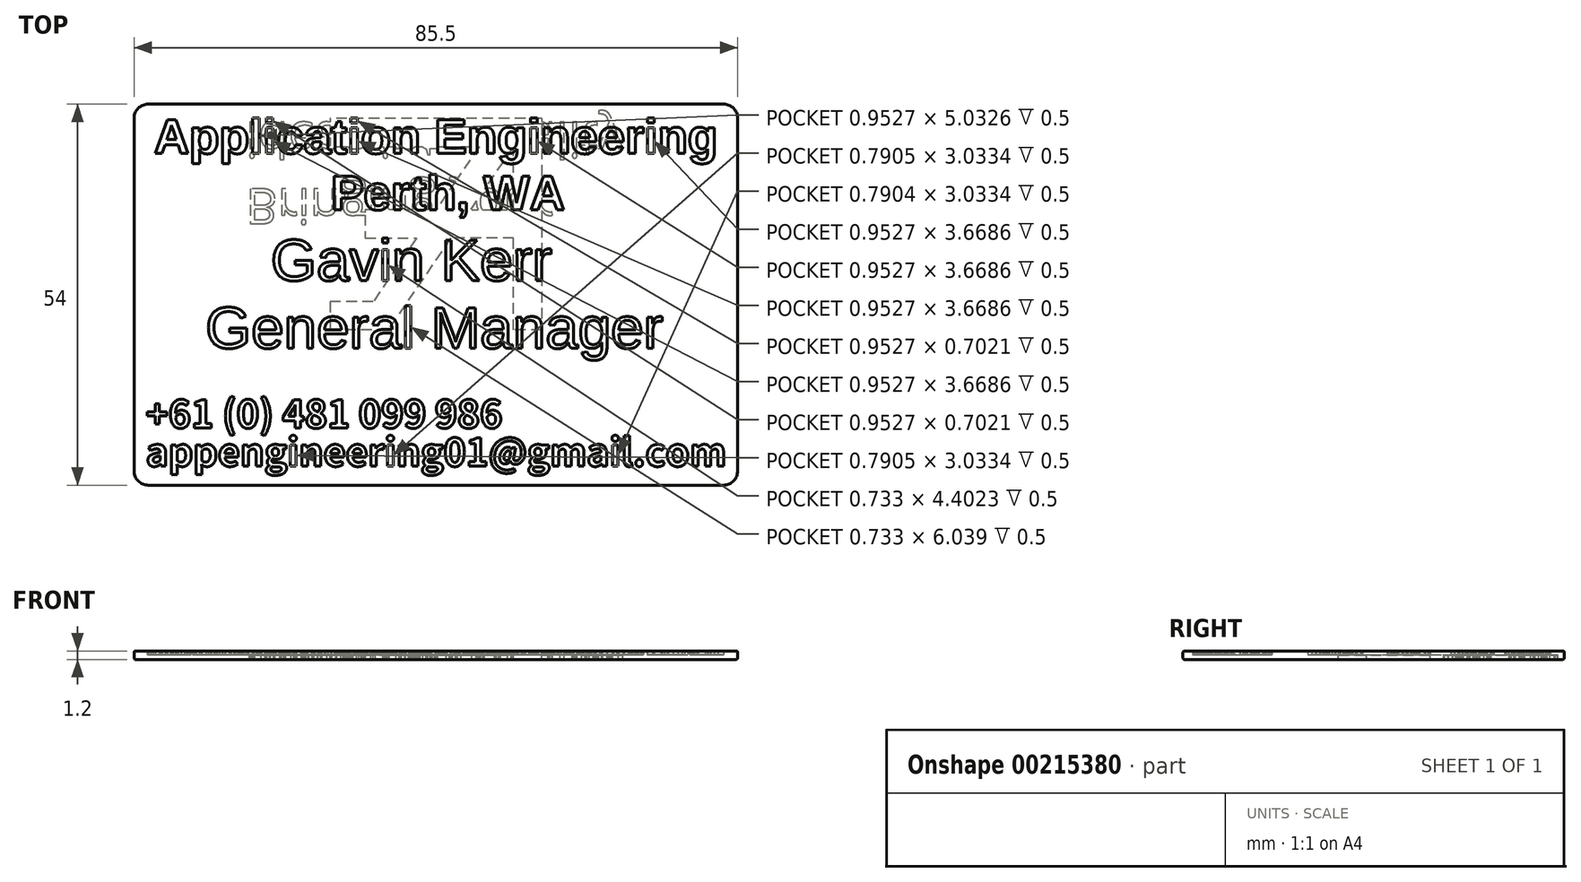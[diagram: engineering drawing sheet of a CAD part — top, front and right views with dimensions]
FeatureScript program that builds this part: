
annotation { "Feature Type Name" : "Feature", "Feature Type Description" : "" }
export const myFeature = defineFeature(function(context is Context, id is Id, definition is map)
    precondition{}
    {
        {
            var Q0;
            Q0=qCreatedBy(makeId("Top.planeOp"),FACE);
            var sketch = newSketch(context, id + "F0", { "sketchPlane" : qUnion([Q0])});
            skLineSegment(sketch, "E0.bottom", {"start": v(40.75, 27) * mm, "end": v(-40.75, 27) * mm});
            skLineSegment(sketch, "E0.top", {"start": v(40.75, -27) * mm, "end": v(-40.75, -27) * mm});
            skLineSegment(sketch, "E0.left", {"start": v(42.75, 25) * mm, "end": v(42.75, -25) * mm});
            skLineSegment(sketch, "E0.right", {"start": v(-42.75, 25) * mm, "end": v(-42.75, -25) * mm});
            skPoint(sketch, "E0.middle", {"position": v(0, 0) * mm});
            skPoint(sketch, "E1.visualSharp", {"position": v(-42.75, 27) * mm});
            skArc(sketch, "E1.filletArc", {"start": v(-40.75, 27) * mm, "mid": v(-42.16, 26.41) * mm, "end": v(-42.75, 25) * mm});
            skPoint(sketch, "E2.visualSharp", {"position": v(42.75, 27) * mm});
            skArc(sketch, "E2.filletArc", {"start": v(42.75, 25) * mm, "mid": v(42.16, 26.41) * mm, "end": v(40.75, 27) * mm});
            skPoint(sketch, "E3.visualSharp", {"position": v(42.75, -27) * mm});
            skArc(sketch, "E3.filletArc", {"start": v(40.75, -27) * mm, "mid": v(42.16, -26.41) * mm, "end": v(42.75, -25) * mm});
            skPoint(sketch, "E4.visualSharp", {"position": v(-42.75, -27) * mm});
            skArc(sketch, "E4.filletArc", {"start": v(-42.75, -25) * mm, "mid": v(-42.16, -26.41) * mm, "end": v(-40.75, -27) * mm});
            skSolve(sketch);
        }
        {
            var Q0;
            Q0=qSketchRegion(id+"F0",true);
            extrude(context, id + "F1", {"entities" : qUnion([Q0]), "endBound" : BoundingType.SYMMETRIC, "depth" : 1.2 * mm});
        }
        {
            var Q0;
            Q0=makeQuery(id+"F1.opExtrude","CAP_EDGE",EDGE,{"disambiguationData":[OSD([sQuery(id+"F0.wireOp",EDGE,"E0.bottom")])],"isStart":false});
            var Q1;
            Q1=makeQuery(id+"F1.opExtrude","CAP_EDGE",EDGE,{"disambiguationData":[OSD([sQuery(id+"F0.wireOp",EDGE,"E0.bottom")])],"isStart":true});
            fillet(context, id + "F2", {"entities" : qUnion([Q0, Q1]), "radius" : .2 * mm, "tangentPropagation" : true, "allowEdgeOverflow" : false});
        }
        {
            var Q0;
            Q0=qCreatedBy(makeId("Top.planeOp"),FACE);
            cPlane(context, id + "F3", {"entities" : qUnion([Q0]), "cplaneType" : CPlaneType.OFFSET, "offset" : .1 * mm, "width" : 150 * mm, "height" : 150 * mm});
        }
        {
            var Q0;
            Q0=qCreatedBy(id+"F3.planeOp",FACE);
            var sketch = newSketch(context, id + "F4", { "sketchPlane" : qUnion([Q0])});
            skText(sketch, "E5", { "text": "Application Engineering\n             Perth, WA", "fontName": "Arimo-Bold.ttf"});
            const initialGuessF4  = {"E5": [-0.03994, 0.02, 1, 0, 0.005]};
            skSetInitialGuess(sketch, initialGuessF4);
            skSolve(sketch);
        }
        {
            var Q0;
            Q0=qCreatedBy(id+"F3.planeOp",FACE);
            var sketch = newSketch(context, id + "F5", { "sketchPlane" : qUnion([Q0])});
            skText(sketch, "E6", { "text": "    Gavin Kerr\nGeneral Manager", "fontName": "Arimo-Regular.ttf"});
            const initialGuessF5  = {"E6": [-0.03264, 0.002, 1, 0, 0.006]};
            skSetInitialGuess(sketch, initialGuessF5);
            skSolve(sketch);
        }
        {
            var Q0;
            Q0=qCreatedBy(id+"F3.planeOp",FACE);
            var sketch = newSketch(context, id + "F6", { "sketchPlane" : qUnion([Q0])});
            skText(sketch, "E7", { "text": "+61 (0) 481 099 986\<email>", "fontName": "NotoSansCJKsc-Bold.otf"});
            const initialGuessF6  = {"E7": [-0.04107, -0.0189, 1, 0, 0.0039]};
            skSetInitialGuess(sketch, initialGuessF6);
            skSolve(sketch);
        }
        {
            var Q0;
            Q0 = qSketchRegion(id + "F4", true);
            var Q1;
            Q1 = qSketchRegion(id + "F5", true);
            var Q2;
            Q2 = qSketchRegion(id + "F6", true);
            extrude(context, id + "F7", {"entities" : qUnion([Q0, Q1, Q2]), "operationType" : NewBodyOperationType.REMOVE, "depth" : .8 * mm});
        }
        {
            var Q0;
            Q0=qCreatedBy(makeId("Top.planeOp"),FACE);
            var sketch = newSketch(context, id + "F8", { "sketchPlane" : qUnion([Q0])});
            skLineSegment(sketch, "E8", {"start": v(0, -50.5) * mm, "end": v(0, 55.1) * mm, "construction": true});
            skSolve(sketch);
        }
        {
            var Q0;
            Q0=sQuery(id+"F8.wireOp",EDGE,"E8");
            cPlane(context, id + "F9", {"entities" : qUnion([Q0]), "cplaneType" : CPlaneType.LINE_ANGLE, "offset" : 25 * mm, "angle" : 180 * degree, "width" : 150 * mm, "height" : 150 * mm});
        }
        {
            var Q0;
            Q0=qCreatedBy(id+"F9.planeOp",FACE);
            var sketch = newSketch(context, id + "F10", { "sketchPlane" : qUnion([Q0])});
            skLineSegment(sketch, "E9", {"start": v(15, -25) * mm, "end": v(15, 5) * mm});
            skLineSegment(sketch, "E10", {"start": v(15, 5) * mm, "end": v(11, 5) * mm});
            skLineSegment(sketch, "E11", {"start": v(11, 5) * mm, "end": v(11, -8) * mm});
            skLineSegment(sketch, "E12", {"start": v(11, -8) * mm, "end": v(2.11, -8) * mm});
            skLineSegment(sketch, "E13", {"start": v(2.11, -8) * mm, "end": v(-6.78, 5) * mm});
            skLineSegment(sketch, "E14", {"start": v(-6.78, 5) * mm, "end": v(-15, 5) * mm});
            skLineSegment(sketch, "E15", {"start": v(15, -25) * mm, "end": v(-15, -25) * mm});
            skLineSegment(sketch, "E16", {"start": v(-15, -25) * mm, "end": v(-15, -21) * mm});
            skLineSegment(sketch, "E17", {"start": v(-15, -21) * mm, "end": v(6.15, -21) * mm});
            skLineSegment(sketch, "E18", {"start": v(6.15, -21) * mm, "end": v(0, -12) * mm});
            skLineSegment(sketch, "E19", {"start": v(0, -12) * mm, "end": v(-10, -12) * mm});
            skLineSegment(sketch, "E20", {"start": v(-10, -12) * mm, "end": v(-10, -8) * mm});
            skLineSegment(sketch, "E21", {"start": v(-10, -8) * mm, "end": v(-2.74, -8) * mm});
            skLineSegment(sketch, "E22", {"start": v(-2.74, -8) * mm, "end": v(-8.89, 1) * mm});
            skLineSegment(sketch, "E23", {"start": v(-8.89, 1) * mm, "end": v(-15, 1) * mm});
            skLineSegment(sketch, "E24", {"start": v(11, -12) * mm, "end": v(11, -21) * mm});
            skLineSegment(sketch, "E25", {"start": v(11, -21) * mm, "end": v(4.85, -12) * mm});
            skLineSegment(sketch, "E26", {"start": v(4.85, -12) * mm, "end": v(11, -12) * mm});
            skLineSegment(sketch, "E27", {"start": v(-15, 1) * mm, "end": v(-15, 5) * mm});
            skPoint(sketch, "E28.middle", {"position": v(0, -10) * mm});
            skSolve(sketch);
        }
        {
            var Q0;
            Q0=qCreatedBy(id+"F9.planeOp",FACE);
            var sketch = newSketch(context, id + "F11", { "sketchPlane" : qUnion([Q0])});
            skText(sketch, "E29", { "text": "Bringing your\nideas into reality", "fontName": "OpenSans-Regular.ttf"});
            const initialGuessF11  = {"E29": [-0.02693, -0.015, 1, 0, 0.005]};
            skSetInitialGuess(sketch, initialGuessF11);
            skSolve(sketch);
        }
        {
            var Q0;
            Q0 = qSketchRegion(id + "F10", true);
            var Q1;
            Q1 = qSketchRegion(id + "F11", true);
            extrude(context, id + "F12", {"entities" : qUnion([Q0, Q1]), "operationType" : NewBodyOperationType.REMOVE, "depth" : .8 * mm});
        }
    });
